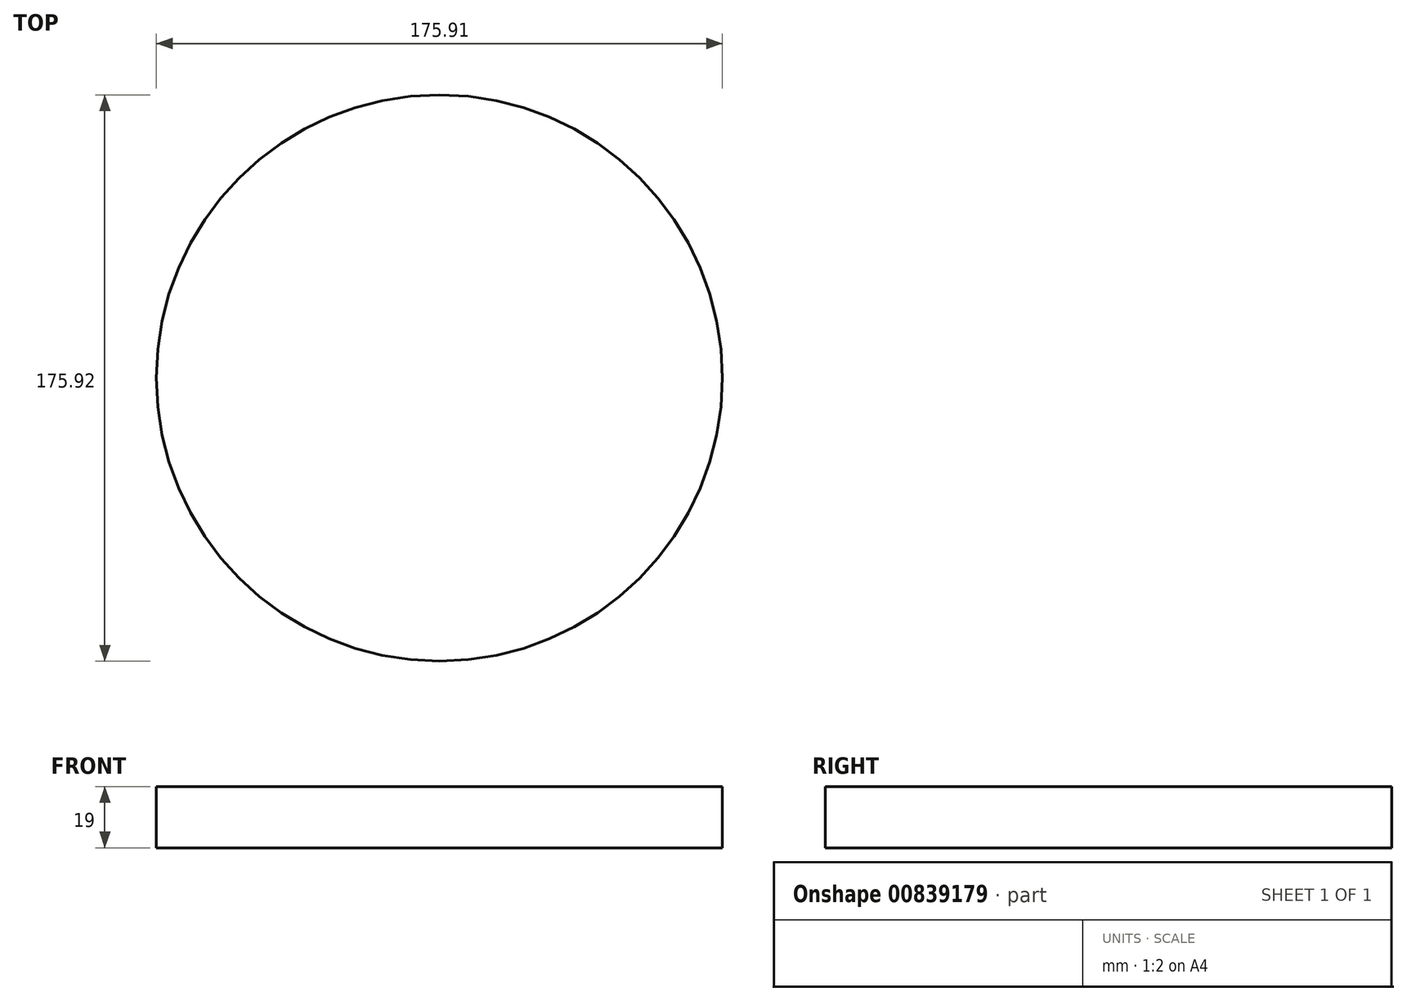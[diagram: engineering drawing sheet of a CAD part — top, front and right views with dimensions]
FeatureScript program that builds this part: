
annotation { "Feature Type Name" : "Feature", "Feature Type Description" : "" }
export const myFeature = defineFeature(function(context is Context, id is Id, definition is map)
    precondition{}
    {
        {
            var Q0;
            Q0=qCreatedBy(makeId("Top.planeOp"),FACE);
            var sketch = newSketch(context, id + "F0", { "sketchPlane" : qUnion([Q0])});
            skCircle(sketch, "E0", {"center": v(-199.58, 18.52) * mm, "radius": 87.96 * mm});
            skSolve(sketch);
        }
        {
            var Q0;
            Q0=makeQuery(id+"F0.imprint","IMPRINT",FACE,{"disambiguationData":[TD([[makeQuery(id+"F0.imprint","IMPRINT",EDGE,{"derivedFrom":sQuery(id+"F0.wireOp",EDGE,"E0")}),1.0]])]});
            extrude(context, id + "F1", {"entities" : qUnion([Q0]), "depth" : 19 * mm, "offsetDistance" : 25.4 * mm});
        }
    });
